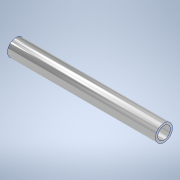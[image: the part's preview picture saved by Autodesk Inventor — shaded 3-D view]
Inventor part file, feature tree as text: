
AUTODESK INVENTOR PART (.ipt)
format: ipt  version: 2020.3 (Build 243373000, 373)  size: 100,352 bytes
history: native  units: mm
features: other x1, extrude x1, sketch x1
ambient origin geometry x8: Origin, YZ Plane, XZ Plane, XY Plane, X Axis, Y Axis, Z Axis, Center Point
bodies: Body1 (feature_tree)
feature tree (3):
  other  "ソリッド1"
  extrude  "押し出し1"  Depth=4.0mm
  sketch  "スケッチ1"
